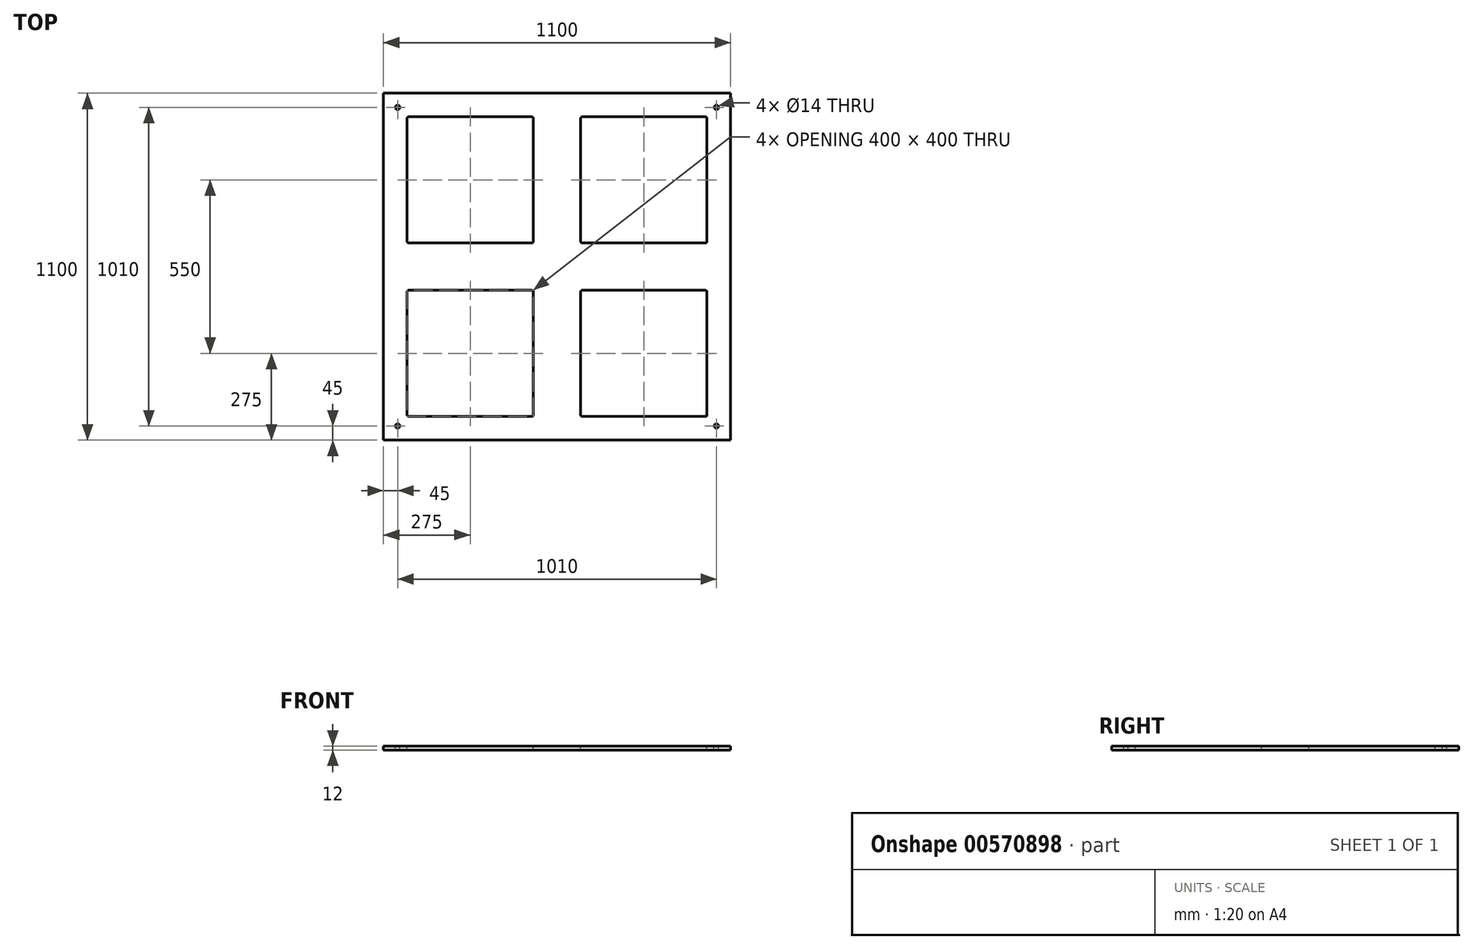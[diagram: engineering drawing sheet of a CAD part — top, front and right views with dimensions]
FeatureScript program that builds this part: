
annotation { "Feature Type Name" : "Feature", "Feature Type Description" : "" }
export const myFeature = defineFeature(function(context is Context, id is Id, definition is map)
    precondition{}
    {
        {
            var Q0;
            Q0=qCreatedBy(makeId("Top.planeOp"),FACE);
            var sketch = newSketch(context, id + "F0", { "sketchPlane" : qUnion([Q0])});
            skLineSegment(sketch, "E0.bottom", {"start": v(-550, 550) * mm, "end": v(550, 550) * mm});
            skLineSegment(sketch, "E0.top", {"start": v(-550, -550) * mm, "end": v(550, -550) * mm});
            skLineSegment(sketch, "E0.left", {"start": v(-550, 550) * mm, "end": v(-550, -550) * mm});
            skLineSegment(sketch, "E0.right", {"start": v(550, 550) * mm, "end": v(550, -550) * mm});
            skSolve(sketch);
        }
        {
            var Q0;
            Q0=makeQuery(id+"F0.imprint","IMPRINT",FACE,{"disambiguationData":[TD([[makeQuery(id+"F0.imprint","IMPRINT",EDGE,{"derivedFrom":sQuery(id+"F0.wireOp",EDGE,"E0.bottom")}),-1.0]])]});
            var Q1;
            Q1=makeQuery(id+"F0.imprint","IMPRINT",FACE,{"disambiguationData":[TD([[makeQuery(id+"F0.imprint","IMPRINT",EDGE,{"derivedFrom":sQuery(id+"F0.wireOp",EDGE,"uFfnzO46-rzXy-thsv-nqKT-xSAOdvmnRc68")}),1.0]])]});
            var Q2;
            Q2=makeQuery(id+"F0.imprint","IMPRINT",FACE,{"disambiguationData":[TD([[makeQuery(id+"F0.imprint","IMPRINT",EDGE,{"derivedFrom":sQuery(id+"F0.wireOp",EDGE,"uFfnzO46-rzXy-thsv-nqKT-xSAOdvmnRc68")}),-1.0]])]});
            extrude(context, id + "F1", {"entities" : qUnion([Q0, Q1, Q2]), "oppositeDirection" : true, "depth" : 12 * mm, "offsetDistance" : 25 * mm});
        }
        {
            var Q0;
            Q0=qCreatedBy(makeId("Top.planeOp"),FACE);
            var sketch = newSketch(context, id + "F2", { "sketchPlane" : qUnion([Q0])});
            skCircle(sketch, "E1", {"center": v(-505, -505) * mm, "radius": 7 * mm});
            skCircle(sketch, "E2", {"center": v(505, -505) * mm, "radius": 7 * mm});
            skCircle(sketch, "E3", {"center": v(505, 505) * mm, "radius": 7 * mm});
            skCircle(sketch, "E4", {"center": v(-505, 505) * mm, "radius": 7 * mm});
            skSolve(sketch);
        }
        {
            var Q0;
            Q0=makeQuery(id+"F2.imprint","IMPRINT",FACE,{"disambiguationData":[TD([[makeQuery(id+"F2.imprint","IMPRINT",EDGE,{"derivedFrom":sQuery(id+"F2.wireOp",EDGE,"E1")}),1.0]])]});
            var Q1;
            Q1=makeQuery(id+"F2.imprint","IMPRINT",FACE,{"disambiguationData":[TD([[makeQuery(id+"F2.imprint","IMPRINT",EDGE,{"derivedFrom":sQuery(id+"F2.wireOp",EDGE,"E3")}),1.0]])]});
            var Q2;
            Q2=makeQuery(id+"F2.imprint","IMPRINT",FACE,{"disambiguationData":[TD([[makeQuery(id+"F2.imprint","IMPRINT",EDGE,{"derivedFrom":sQuery(id+"F2.wireOp",EDGE,"E4")}),1.0]])]});
            var Q3;
            Q3=makeQuery(id+"F2.imprint","IMPRINT",FACE,{"disambiguationData":[TD([[makeQuery(id+"F2.imprint","IMPRINT",EDGE,{"derivedFrom":sQuery(id+"F2.wireOp",EDGE,"E2")}),1.0]])]});
            var Q4;
            Q4=sQuery(id+"F2.wireOp",EDGE,"E1");
            extrude(context, id + "F3", {"entities" : qUnion([Q0, Q1, Q2, Q3]), "operationType" : NewBodyOperationType.REMOVE, "surfaceEntities" : qUnion([Q4]), "oppositeDirection" : true, "depth" : 25 * mm, "offsetDistance" : 25 * mm});
        }
        {
            var Q0;
            Q0=qCreatedBy(makeId("Top.planeOp"),FACE);
            var sketch = newSketch(context, id + "F4", { "sketchPlane" : qUnion([Q0])});
            skLineSegment(sketch, "E5.bottom", {"start": v(-470, 475) * mm, "end": v(-80, 475) * mm});
            skLineSegment(sketch, "E5.top", {"start": v(-470, 75) * mm, "end": v(-80, 75) * mm});
            skLineSegment(sketch, "E5.left", {"start": v(-475, 470) * mm, "end": v(-475, 80) * mm});
            skLineSegment(sketch, "E5.right", {"start": v(-75, 470) * mm, "end": v(-75, 80) * mm});
            skLineSegment(sketch, "E6.MirrorCS", {"start": v(75, 470) * mm, "end": v(75, 80) * mm});
            skLineSegment(sketch, "E7.MirrorCS", {"start": v(470, 475) * mm, "end": v(80, 475) * mm});
            skLineSegment(sketch, "E8.MirrorCS", {"start": v(475, 470) * mm, "end": v(475, 80) * mm});
            skLineSegment(sketch, "E9.MirrorCS", {"start": v(470, 75) * mm, "end": v(80, 75) * mm});
            skLineSegment(sketch, "E10.MirrorCS", {"start": v(470, -75) * mm, "end": v(80, -75) * mm});
            skLineSegment(sketch, "E11.MirrorCS", {"start": v(470, -475) * mm, "end": v(80, -475) * mm});
            skLineSegment(sketch, "E12.MirrorCS", {"start": v(75, -470) * mm, "end": v(75, -80) * mm});
            skLineSegment(sketch, "E13.MirrorCS", {"start": v(475, -470) * mm, "end": v(475, -80) * mm});
            skLineSegment(sketch, "E14.MirrorCS", {"start": v(-470, -475) * mm, "end": v(-80, -475) * mm});
            skLineSegment(sketch, "E15.MirrorCS", {"start": v(-75, -470) * mm, "end": v(-75, -80) * mm});
            skLineSegment(sketch, "E16.MirrorCS", {"start": v(-470, -75) * mm, "end": v(-80, -75) * mm});
            skLineSegment(sketch, "E17.MirrorCS", {"start": v(-475, -470) * mm, "end": v(-475, -80) * mm});
            skPoint(sketch, "E18.visualSharp", {"position": v(-475, 475) * mm});
            skArc(sketch, "E18.filletArc", {"start": v(-470, 475) * mm, "mid": v(-473.54, 473.54) * mm, "end": v(-475, 470) * mm});
            skPoint(sketch, "E19.visualSharp", {"position": v(-75, 475) * mm});
            skArc(sketch, "E19.filletArc", {"start": v(-75, 470) * mm, "mid": v(-76.46, 473.54) * mm, "end": v(-80, 475) * mm});
            skPoint(sketch, "E20.visualSharp", {"position": v(-75, 75) * mm});
            skArc(sketch, "E20.filletArc", {"start": v(-80, 75) * mm, "mid": v(-76.46, 76.46) * mm, "end": v(-75, 80) * mm});
            skPoint(sketch, "E21.visualSharp", {"position": v(-475, 75) * mm});
            skArc(sketch, "E21.filletArc", {"start": v(-475, 80) * mm, "mid": v(-473.54, 76.46) * mm, "end": v(-470, 75) * mm});
            skPoint(sketch, "E22.visualSharp", {"position": v(75, 475) * mm});
            skArc(sketch, "E22.filletArc", {"start": v(80, 475) * mm, "mid": v(76.46, 473.54) * mm, "end": v(75, 470) * mm});
            skPoint(sketch, "E23.visualSharp", {"position": v(475, 475) * mm});
            skArc(sketch, "E23.filletArc", {"start": v(475, 470) * mm, "mid": v(473.54, 473.54) * mm, "end": v(470, 475) * mm});
            skPoint(sketch, "E24.visualSharp", {"position": v(475, 75) * mm});
            skArc(sketch, "E24.filletArc", {"start": v(470, 75) * mm, "mid": v(473.54, 76.46) * mm, "end": v(475, 80) * mm});
            skPoint(sketch, "E25.visualSharp", {"position": v(75, 75) * mm});
            skArc(sketch, "E25.filletArc", {"start": v(75, 80) * mm, "mid": v(76.46, 76.46) * mm, "end": v(80, 75) * mm});
            skPoint(sketch, "E26.visualSharp", {"position": v(75, -75) * mm});
            skArc(sketch, "E26.filletArc", {"start": v(80, -75) * mm, "mid": v(76.46, -76.46) * mm, "end": v(75, -80) * mm});
            skPoint(sketch, "E27.visualSharp", {"position": v(475, -75) * mm});
            skArc(sketch, "E27.filletArc", {"start": v(475, -80) * mm, "mid": v(473.54, -76.46) * mm, "end": v(470, -75) * mm});
            skPoint(sketch, "E28.visualSharp", {"position": v(475, -475) * mm});
            skArc(sketch, "E28.filletArc", {"start": v(470, -475) * mm, "mid": v(473.54, -473.54) * mm, "end": v(475, -470) * mm});
            skPoint(sketch, "E29.visualSharp", {"position": v(75, -475) * mm});
            skArc(sketch, "E29.filletArc", {"start": v(75, -470) * mm, "mid": v(76.46, -473.54) * mm, "end": v(80, -475) * mm});
            skPoint(sketch, "E30.visualSharp", {"position": v(-75, -75) * mm});
            skArc(sketch, "E30.filletArc", {"start": v(-75, -80) * mm, "mid": v(-76.46, -76.46) * mm, "end": v(-80, -75) * mm});
            skPoint(sketch, "E31.visualSharp", {"position": v(-475, -75) * mm});
            skArc(sketch, "E31.filletArc", {"start": v(-470, -75) * mm, "mid": v(-473.54, -76.46) * mm, "end": v(-475, -80) * mm});
            skPoint(sketch, "E32.visualSharp", {"position": v(-475, -475) * mm});
            skArc(sketch, "E32.filletArc", {"start": v(-475, -470) * mm, "mid": v(-473.54, -473.54) * mm, "end": v(-470, -475) * mm});
            skPoint(sketch, "E33.visualSharp", {"position": v(-75, -475) * mm});
            skArc(sketch, "E33.filletArc", {"start": v(-80, -475) * mm, "mid": v(-76.46, -473.54) * mm, "end": v(-75, -470) * mm});
            skSolve(sketch);
        }
        {
            var Q0;
            Q0 = qSketchRegion(id + "F4", true);
            extrude(context, id + "F5", {"entities" : qUnion([Q0]), "operationType" : NewBodyOperationType.REMOVE, "oppositeDirection" : true, "depth" : 25 * mm, "offsetDistance" : 25 * mm});
        }
    });
